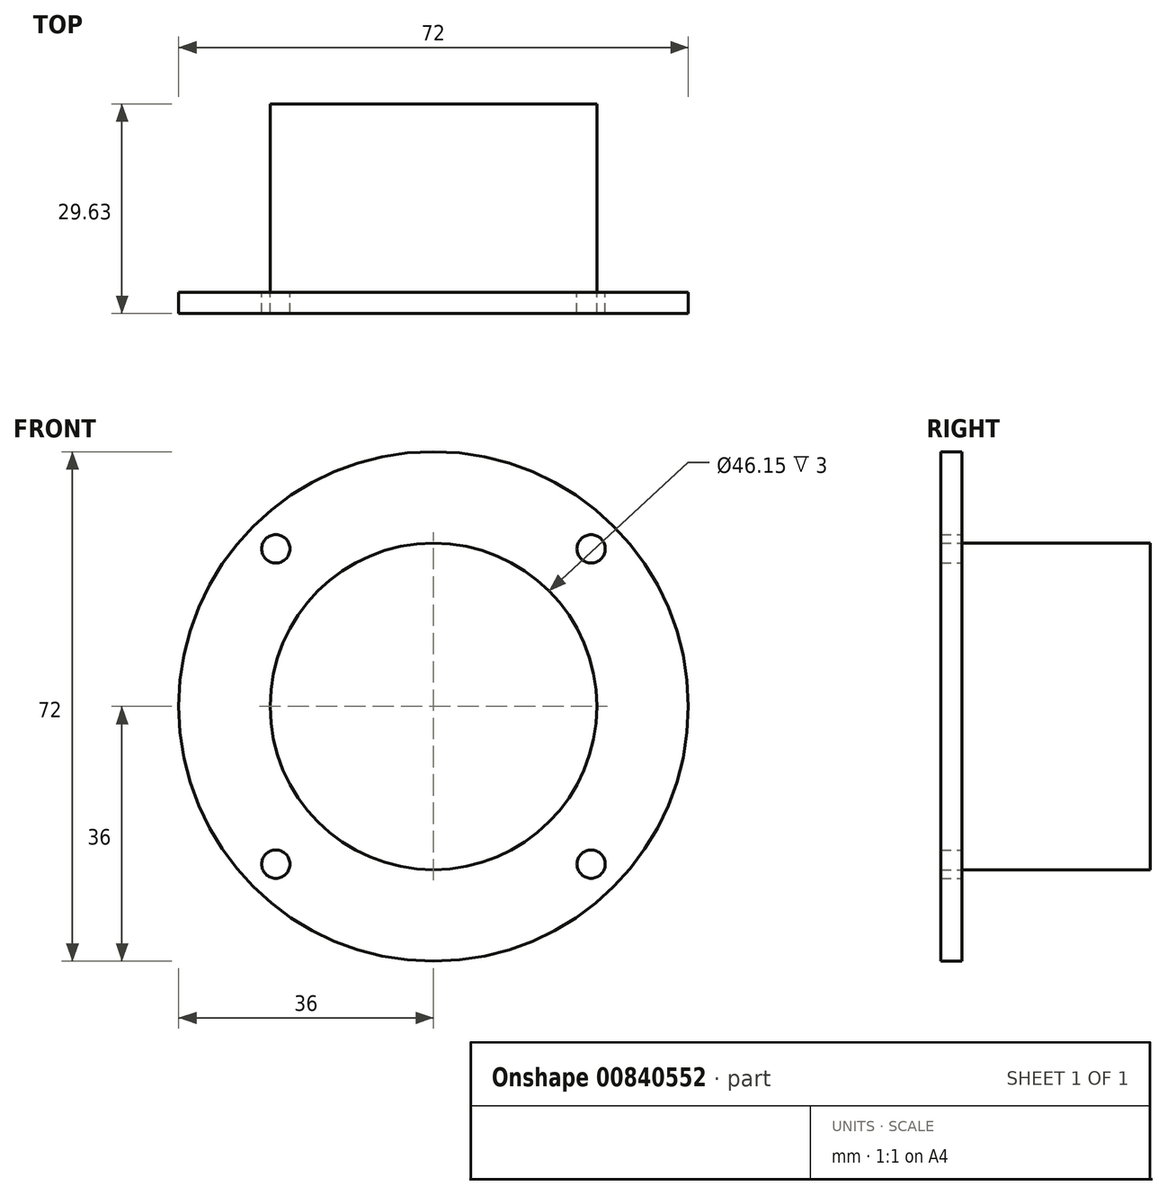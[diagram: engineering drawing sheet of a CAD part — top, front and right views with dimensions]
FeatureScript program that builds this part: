
annotation { "Feature Type Name" : "Feature", "Feature Type Description" : "" }
export const myFeature = defineFeature(function(context is Context, id is Id, definition is map)
    precondition{}
    {
        {
            var Q0;
            Q0=qCreatedBy(makeId("Front.planeOp"),FACE);
            var sketch = newSketch(context, id + "F0", { "sketchPlane" : qUnion([Q0])});
            skCircle(sketch, "E0", {"center": v(0, 0) * mm, "radius": 36 * mm});
            skCircle(sketch, "E1", {"center": v(0, 0) * mm, "radius": 31.5 * mm});
            skCircle(sketch, "E2", {"center": v(0, 0) * mm, "radius": 23.07 * mm});
            skLineSegment(sketch, "E3", {"start": v(0, 0) * mm, "end": v(22.27, 22.27) * mm, "construction": true});
            skLineSegment(sketch, "E4", {"start": v(0, 0) * mm, "end": v(-22.27, 22.27) * mm, "construction": true});
            skLineSegment(sketch, "E5", {"start": v(0, 0) * mm, "end": v(22.27, -22.27) * mm, "construction": true});
            skLineSegment(sketch, "E6", {"start": v(0, 0) * mm, "end": v(-22.27, -22.27) * mm, "construction": true});
            skCircle(sketch, "E7", {"center": v(-22.27, 22.27) * mm, "radius": 2 * mm});
            skCircle(sketch, "E8", {"center": v(22.27, -22.27) * mm, "radius": 2 * mm});
            skCircle(sketch, "E9", {"center": v(22.27, 22.27) * mm, "radius": 2 * mm});
            skCircle(sketch, "E10", {"center": v(-22.27, -22.27) * mm, "radius": 2 * mm});
            skSolve(sketch);
        }
        {
            var Q0;
            Q0=makeQuery(id+"F0.imprint","IMPRINT",FACE,{"disambiguationData":[TD([[makeQuery(id+"F0.imprint","IMPRINT",EDGE,{"derivedFrom":sQuery(id+"F0.wireOp",EDGE,"E0")}),1.0]])]});
            var Q1;
            Q1=makeQuery(id+"F0.imprint","IMPRINT",FACE,{"disambiguationData":[TD([[makeQuery(id+"F0.imprint","IMPRINT",EDGE,{"derivedFrom":sQuery(id+"F0.wireOp",EDGE,"E2")}),-1.0]])]});
            extrude(context, id + "F1", {"entities" : qUnion([Q0, Q1]), "depth" : 3 * mm, "offsetDistance" : 25 * mm});
        }
        {
            var Q0;
            Q0=makeQuery(id+"F0.imprint","IMPRINT",FACE,{"disambiguationData":[TD([[makeQuery(id+"F0.imprint","IMPRINT",EDGE,{"derivedFrom":sQuery(id+"F0.wireOp",EDGE,"E2")}),1.0]])]});
            extrude(context, id + "F2", {"entities" : qUnion([Q0]), "depth" : -26.63 * mm, "offsetDistance" : 25 * mm});
        }
    });
